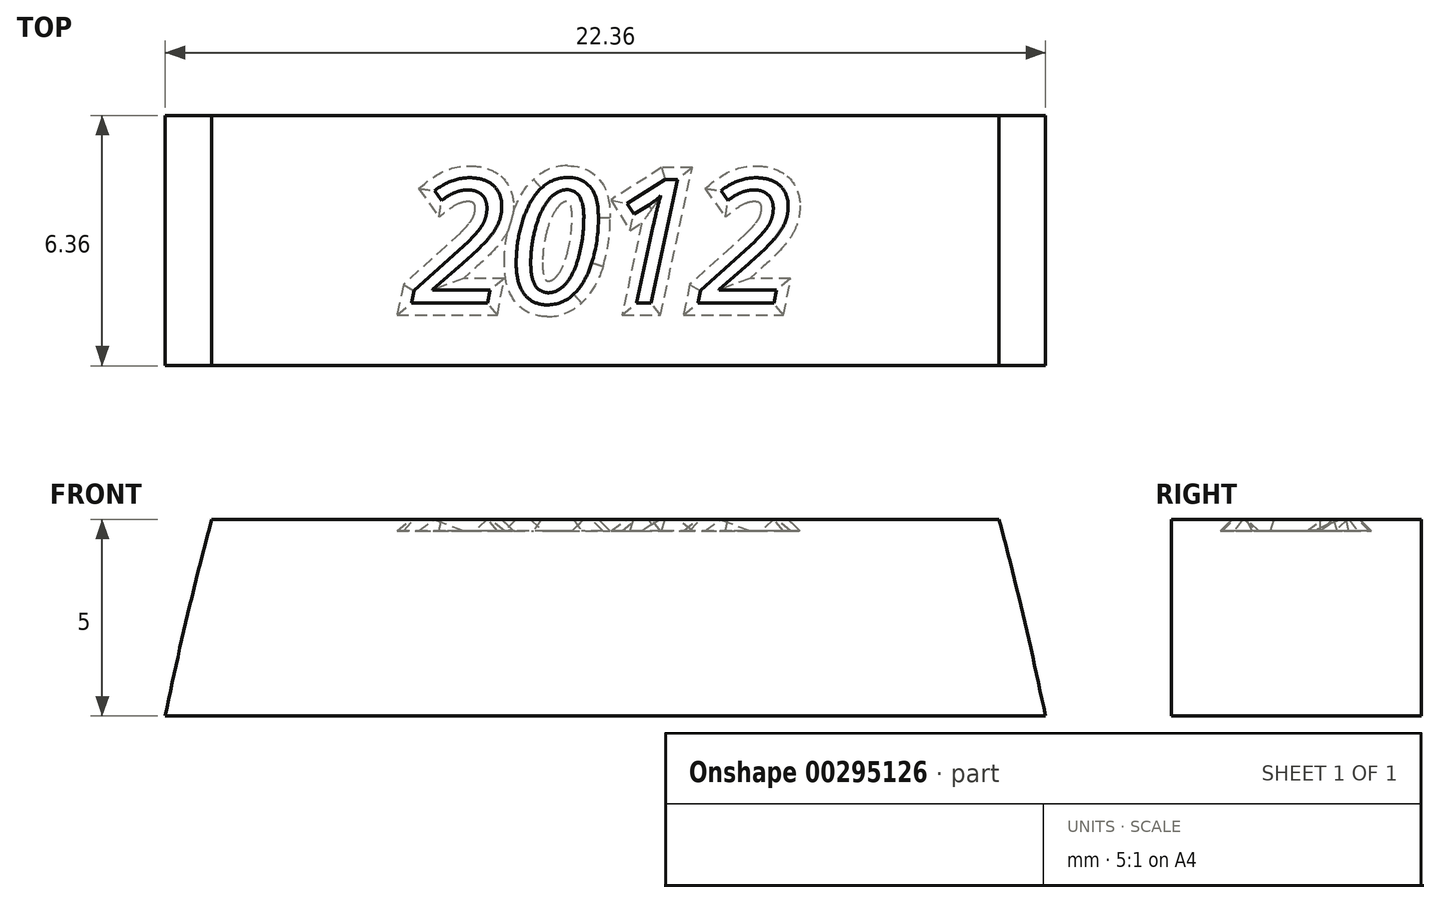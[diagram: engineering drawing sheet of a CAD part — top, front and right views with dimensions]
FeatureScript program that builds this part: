
annotation { "Feature Type Name" : "Feature", "Feature Type Description" : "" }
export const myFeature = defineFeature(function(context is Context, id is Id, definition is map)
    precondition{}
    {
        {
            var Q0;
            Q0=qCreatedBy(makeId("Front.planeOp"),FACE);
            var sketch = newSketch(context, id + "F0", { "sketchPlane" : qUnion([Q0])});
            skCircle(sketch, "E0", {"center": v(0, 0) * mm, "radius": 8.5 * mm});
            skCircle(sketch, "E1", {"center": v(0, 0) * mm, "radius": 11.5 * mm});
            skSolve(sketch);
        }
        {
            var Q0;
            Q0=qCreatedBy(makeId("Front.planeOp"),FACE);
            var sketch = newSketch(context, id + "F1", { "sketchPlane" : qUnion([Q0])});
            skLineSegment(sketch, "E2", {"start": v(-10, 16.5) * mm, "end": v(10, 16.5) * mm});
            skLineSegment(sketch, "E3", {"start": v(-8.5, 0) * mm, "end": v(-11.5, 0) * mm, "construction": true});
            skLineSegment(sketch, "E4", {"start": v(-10, 16.5) * mm, "end": v(-10, 0) * mm, "construction": true});
            skLineSegment(sketch, "E5", {"start": v(-10, 16.5) * mm, "end": v(-14.42, 0) * mm, "construction": true});
            skLineSegment(sketch, "E6", {"start": v(0, 0) * mm, "end": v(-9.42, -6.6) * mm, "construction": true});
            skFitSpline(sketch, "E7", {"points": [v(-9.42, -6.6) * mm, v(-12.07, 0) * mm, v(-10, 16.5) * mm], "startDerivative": vector(-9.97, 14.24) * mm, "endDerivative": vector(8.14, 30.38) * mm});
            skLineSegment(sketch, "E8", {"start": v(-9.42, -6.6) * mm, "end": v(-7.7, -9.05) * mm, "construction": true});
            skFitSpline(sketch, "E9.MirrorCS", {"points": [v(9.42, -6.6) * mm, v(12.07, 0) * mm, v(10, 16.5) * mm], "startDerivative": vector(9.97, 14.24) * mm, "endDerivative": vector(-8.14, 30.38) * mm});
            skCircle(sketch, "E10", {"center": v(0, 0) * mm, "radius": 8.5 * mm});
            skArc(sketch, "E11", {"start": v(-9.42, -6.6) * mm, "mid": v(0, -11.5) * mm, "end": v(9.42, -6.6) * mm});
            skSolve(sketch);
        }
        {
            var Q0;
            Q0=qSketchRegion(id+"F1",true);
            extrude(context, id + "F2", {"entities" : qUnion([Q0]), "endBound" : BoundingType.SYMMETRIC, "depth" : 16.75 * mm});
        }
        {
            var Q0;
            Q0=qCreatedBy(makeId("Right.planeOp"),FACE);
            var sketch = newSketch(context, id + "F3", { "sketchPlane" : qUnion([Q0])});
            skLineSegment(sketch, "E12", {"start": v(0, 8.5) * mm, "end": v(-8.38, 8.5) * mm, "construction": true});
            skLineSegment(sketch, "E13", {"start": v(0, -11.5) * mm, "end": v(-3, -11.5) * mm});
            skLineSegment(sketch, "E14", {"start": v(-3, -11.5) * mm, "end": v(-8.38, -11.5) * mm, "construction": true});
            skLineSegment(sketch, "E15", {"start": v(-8.38, 8.5) * mm, "end": v(-7.4, 16.5) * mm, "construction": true});
            skLineSegment(sketch, "E16", {"start": v(-7.4, 16.5) * mm, "end": v(0, 16.5) * mm, "construction": true});
            skLineSegment(sketch, "E17", {"start": v(-7.4, 16.5) * mm, "end": v(-8.38, 16.5) * mm, "construction": true});
            skFitSpline(sketch, "E18", {"points": [v(-7.4, 16.5) * mm, v(-8.38, 8.5) * mm, v(-3, -11.5) * mm], "startDerivative": vector(-2.37, -19.33) * mm, "endDerivative": vector(15.27, -41.97) * mm});
            skLineSegment(sketch, "E19", {"start": v(-3, -11.5) * mm, "end": v(0, -19.74) * mm});
            skLineSegment(sketch, "E20", {"start": v(-7.4, 16.5) * mm, "end": v(0, 23.23) * mm});
            skLineSegment(sketch, "E21.MirrorCS", {"start": v(7.4, 16.5) * mm, "end": v(0, 23.23) * mm});
            skFitSpline(sketch, "E22.MirrorCS", {"points": [v(7.4, 16.5) * mm, v(8.38, 8.5) * mm, v(3, -11.5) * mm], "startDerivative": vector(2.37, -19.33) * mm, "endDerivative": vector(-15.27, -41.97) * mm});
            skLineSegment(sketch, "E23.MirrorCS", {"start": v(3, -11.5) * mm, "end": v(0, -19.74) * mm});
            skSolve(sketch);
        }
        {
            var Q0;
            Q0=qSketchRegion(id+"F3",true);
            extrude(context, id + "F4", {"entities" : qUnion([Q0]), "operationType" : NewBodyOperationType.INTERSECT, "endBound" : BoundingType.SYMMETRIC, "depth" : 50 * mm});
        }
        {
            var Q0;
            Q0=qCreatedBy(makeId("Front.planeOp"),FACE);
            var sketch = newSketch(context, id + "F5", { "sketchPlane" : qUnion([Q0])});
            skCircle(sketch, "E24", {"center": v(0, 0) * mm, "radius": 9.25 * mm});
            skSolve(sketch);
        }
        {
            var Q0;
            Q0=qSketchRegion(id+"F5",true);
            extrude(context, id + "F6", {"entities" : qUnion([Q0]), "operationType" : NewBodyOperationType.REMOVE, "endBound" : BoundingType.SYMMETRIC, "depth" : 50 * mm});
        }
        {
            var Q0;
            Q0=qCreatedBy(makeId("Front.planeOp"),FACE);
            cPlane(context, id + "F7", {"entities" : qUnion([Q0]), "cplaneType" : CPlaneType.OFFSET, "offset" : 2.5 * mm, "width" : 150 * mm, "height" : 150 * mm});
        }
        {
            var Q0;
            Q0=qCreatedBy(id+"F7.planeOp",FACE);
            var sketch = newSketch(context, id + "F8", { "sketchPlane" : qUnion([Q0])});
            skCircle(sketch, "E25", {"center": v(0, 0) * mm, "radius": 10 * mm});
            skSolve(sketch);
        }
        {
            var Q0;
            Q0=qSketchRegion(id+"F8",true);
            extrude(context, id + "F9", {"entities" : qUnion([Q0]), "operationType" : NewBodyOperationType.REMOVE, "depth" : 25 * mm});
        }
        {
            var Q0;
            Q0=qCreatedBy(makeId("Front.planeOp"),FACE);
            cPlane(context, id + "F10", {"entities" : qUnion([Q0]), "cplaneType" : CPlaneType.OFFSET, "offset" : 2.5 * mm, "oppositeDirection" : true, "width" : 150 * mm, "height" : 150 * mm});
        }
        {
            var Q0;
            Q0=qCreatedBy(id+"F10.planeOp",FACE);
            var sketch = newSketch(context, id + "F11", { "sketchPlane" : qUnion([Q0])});
            skCircle(sketch, "E26", {"center": v(0, 0) * mm, "radius": 10 * mm});
            skSolve(sketch);
        }
        {
            var Q0;
            Q0=qSketchRegion(id+"F11",true);
            extrude(context, id + "F12", {"entities" : qUnion([Q0]), "operationType" : NewBodyOperationType.REMOVE, "oppositeDirection" : true, "depth" : 25 * mm});
        }
        {
            var Q0;
            Q0=makeQuery(id+"F2.opExtrude","SWEPT_FACE",FACE,{"disambiguationData":[OSD([sQuery(id+"F1.wireOp",EDGE,"E2")])]});
            cPlane(context, id + "F13", {"entities" : qUnion([Q0]), "cplaneType" : CPlaneType.OFFSET, "offset" : 5 * mm, "oppositeDirection" : true, "width" : 150 * mm, "height" : 150 * mm});
        }
        {
            var Q0;
            Q0=qCreatedBy(makeId("Right.planeOp"),FACE);
            var sketch = newSketch(context, id + "F14", { "sketchPlane" : qUnion([Q0])});
            skLineSegment(sketch, "E27.bottom", {"start": v(3.18, 11.5) * mm, "end": v(-3.18, 11.5) * mm});
            skLineSegment(sketch, "E27.left", {"start": v(3.17, 11.5) * mm, "end": v(3.18, 26.5) * mm});
            skLineSegment(sketch, "E27.right", {"start": v(-3.18, 11.5) * mm, "end": v(-3.17, 26.5) * mm});
            skLineSegment(sketch, "E28", {"start": v(-3.17, 26.5) * mm, "end": v(-18.17, 26.5) * mm});
            skLineSegment(sketch, "E29", {"start": v(-18.17, 26.5) * mm, "end": v(-18.17, -18.5) * mm});
            skLineSegment(sketch, "E30", {"start": v(-18.17, -18.5) * mm, "end": v(18.17, -18.5) * mm});
            skLineSegment(sketch, "E31", {"start": v(18.17, -18.5) * mm, "end": v(18.17, 26.5) * mm});
            skLineSegment(sketch, "E32", {"start": v(18.17, 26.5) * mm, "end": v(3.17, 26.5) * mm});
            skSolve(sketch);
        }
        {
            var Q0;
            Q0 = qSketchRegion(id + "F14", true);
            extrude(context, id + "F15", {"entities" : qUnion([Q0]), "operationType" : NewBodyOperationType.REMOVE, "endBound" : BoundingType.SYMMETRIC, "depth" : 40 * mm});
        }
        {
            var Q0;
            Q0=makeQuery(id+"F2.opExtrude","SWEPT_FACE",FACE,{"disambiguationData":[OSD([sQuery(id+"F1.wireOp",EDGE,"E2")])]});
            var sketch = newSketch(context, id + "F16", { "sketchPlane" : qUnion([Q0])});
            skText(sketch, "E33", { "text": "2012", "fontName": "OpenSans-Italic.ttf"});
            const initialGuessF16  = {"E33": [-0.00495, -0.00159, 1, 0, 0.00317]};
            skSetInitialGuess(sketch, initialGuessF16);
            skSolve(sketch);
        }
        {
            var Q0;
            Q0 = qSketchRegion(id + "F16", true);
            extrude(context, id + "F17", {"entities" : qUnion([Q0]), "operationType" : NewBodyOperationType.REMOVE, "oppositeDirection" : true, "depth" : 0.3 * mm, "hasDraft" : true, "draftAngle" : 45 * degree});
        }
    });
